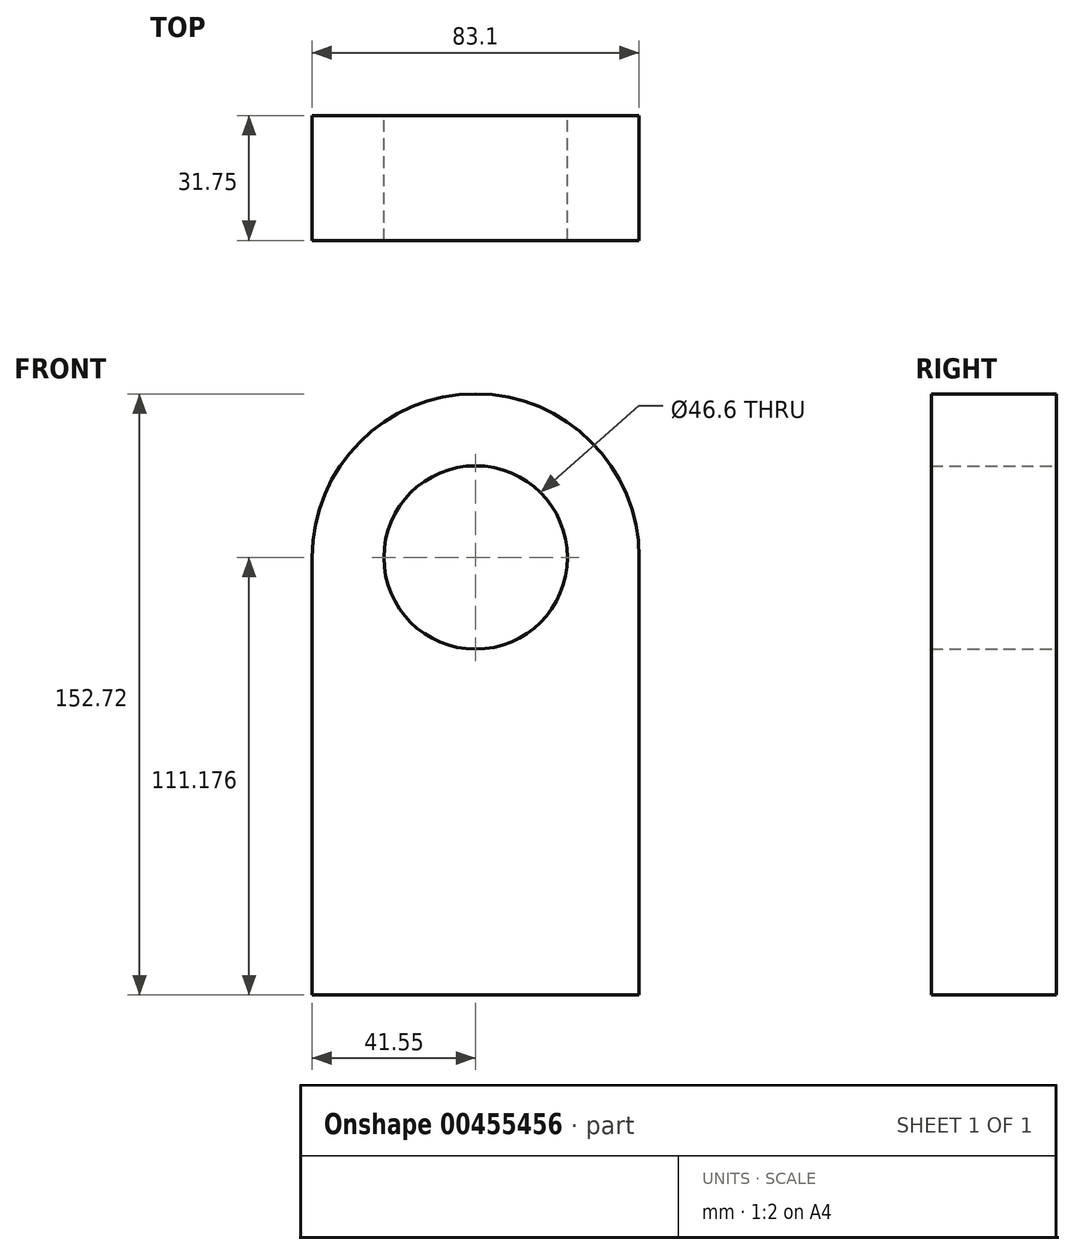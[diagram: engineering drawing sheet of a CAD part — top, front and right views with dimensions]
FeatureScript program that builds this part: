
annotation { "Feature Type Name" : "Feature", "Feature Type Description" : "" }
export const myFeature = defineFeature(function(context is Context, id is Id, definition is map)
    precondition{}
    {
        {
            var Q0;
            Q0=qCreatedBy(makeId("Front.planeOp"),FACE);
            var sketch = newSketch(context, id + "F0", { "sketchPlane" : qUnion([Q0])});
            skLineSegment(sketch, "E0.top", {"start": v(41.55, -55.59) * mm, "end": v(-41.55, -55.59) * mm});
            skLineSegment(sketch, "E0.left", {"start": v(41.55, 55.59) * mm, "end": v(41.55, -55.59) * mm});
            skLineSegment(sketch, "E0.right", {"start": v(-41.55, 55.59) * mm, "end": v(-41.55, -55.59) * mm});
            skPoint(sketch, "E0.middle", {"position": v(0, 0) * mm});
            skArc(sketch, "E1", {"start": v(41.55, 55.59) * mm, "mid": v(0, 97.13) * mm, "end": v(-41.55, 55.59) * mm});
            skArc(sketch, "E2", {"start": v(23.3, 55.59) * mm, "mid": v(0, 32.28) * mm, "end": v(-23.3, 55.59) * mm});
            skArc(sketch, "E3", {"start": v(-23.3, 55.59) * mm, "mid": v(0, 78.89) * mm, "end": v(23.3, 55.59) * mm});
            skSolve(sketch);
        }
        {
            var Q0;
            Q0=makeQuery(id+"F0.imprint","IMPRINT",FACE,{"disambiguationData":[TD([[makeQuery(id+"F0.imprint","IMPRINT",EDGE,{"derivedFrom":sQuery(id+"F0.wireOp",EDGE,"E0.top")}),-1.0]])]});
            extrude(context, id + "F1", {"entities" : qUnion([Q0]), "depth" : 31.75 * mm});
        }
    });
